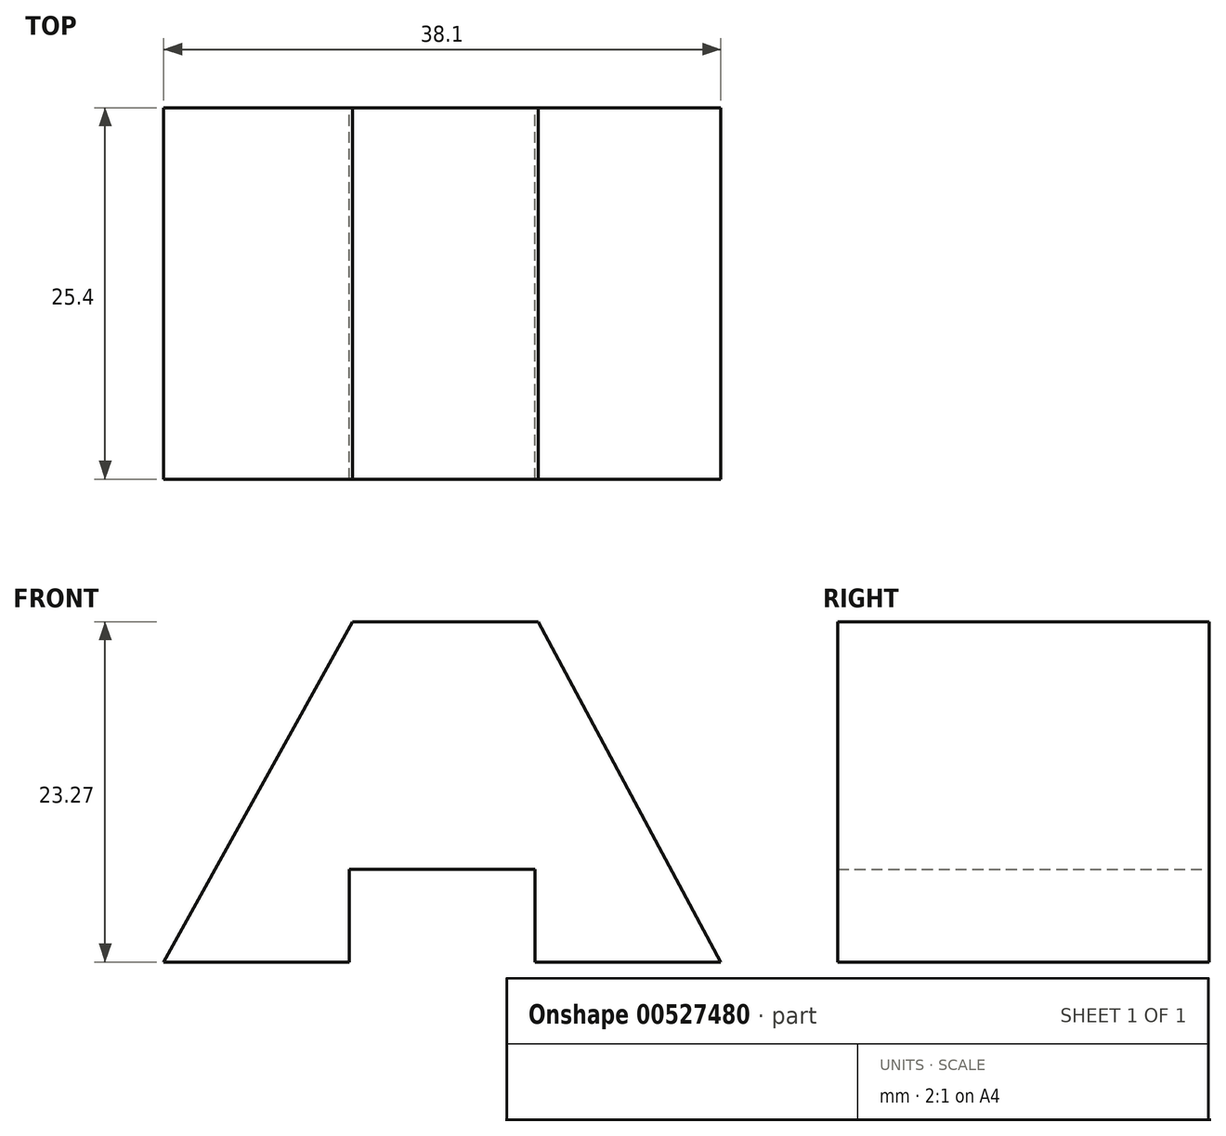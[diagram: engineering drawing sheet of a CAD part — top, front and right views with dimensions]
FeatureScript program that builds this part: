
annotation { "Feature Type Name" : "Feature", "Feature Type Description" : "" }
export const myFeature = defineFeature(function(context is Context, id is Id, definition is map)
    precondition{}
    {
        {
            var Q0;
            Q0=qCreatedBy(makeId("Front.planeOp"),FACE);
            var sketch = newSketch(context, id + "F0", { "sketchPlane" : qUnion([Q0])});
            skLineSegment(sketch, "E0", {"start": v(0, 0) * mm, "end": v(12.9, 23.27) * mm});
            skLineSegment(sketch, "E1", {"start": v(12.9, 23.27) * mm, "end": v(25.6, 23.27) * mm});
            skLineSegment(sketch, "E2", {"start": v(25.6, 23.27) * mm, "end": v(38.1, 0) * mm});
            skLineSegment(sketch, "E3", {"start": v(0, 0) * mm, "end": v(38.1, 0) * mm});
            skSolve(sketch);
        }
        {
            var Q0;
            Q0 = qSketchRegion(id + "F0", true);
            extrude(context, id + "F1", {"entities" : qUnion([Q0]), "depth" : 25.4 * mm, "offsetDistance" : 25.4 * mm});
        }
        {
            var Q0;
            Q0=makeQuery(id+"F1.opExtrude","SWEPT_FACE",FACE,{"disambiguationData":[OSD([sQuery(id+"F0.wireOp",EDGE,"E3")])]});
            var sketch = newSketch(context, id + "F2", { "sketchPlane" : qUnion([Q0])});
            skLineSegment(sketch, "E4", {"start": v(12.7, 25.4) * mm, "end": v(12.7, 0) * mm});
            skLineSegment(sketch, "E5", {"start": v(25.4, 25.4) * mm, "end": v(25.4, 0) * mm});
            skSolve(sketch);
        }
        {
            var Q0;
            {var subQ0=sQuery(id+"F2.wireOp",EDGE,"E4");Q0=makeQuery(id+"F2.imprint","IMPRINT",FACE,{"disambiguationData":[TD([[makeQuery(id+"F2.imprint","IMPRINT",EDGE,{"derivedFrom":subQ0}),1.0]])]});}
            extrude(context, id + "F3", {"entities" : qUnion([Q0]), "operationType" : NewBodyOperationType.REMOVE, "oppositeDirection" : true, "depth" : 6.35 * mm, "offsetDistance" : 25.4 * mm});
        }
    });
